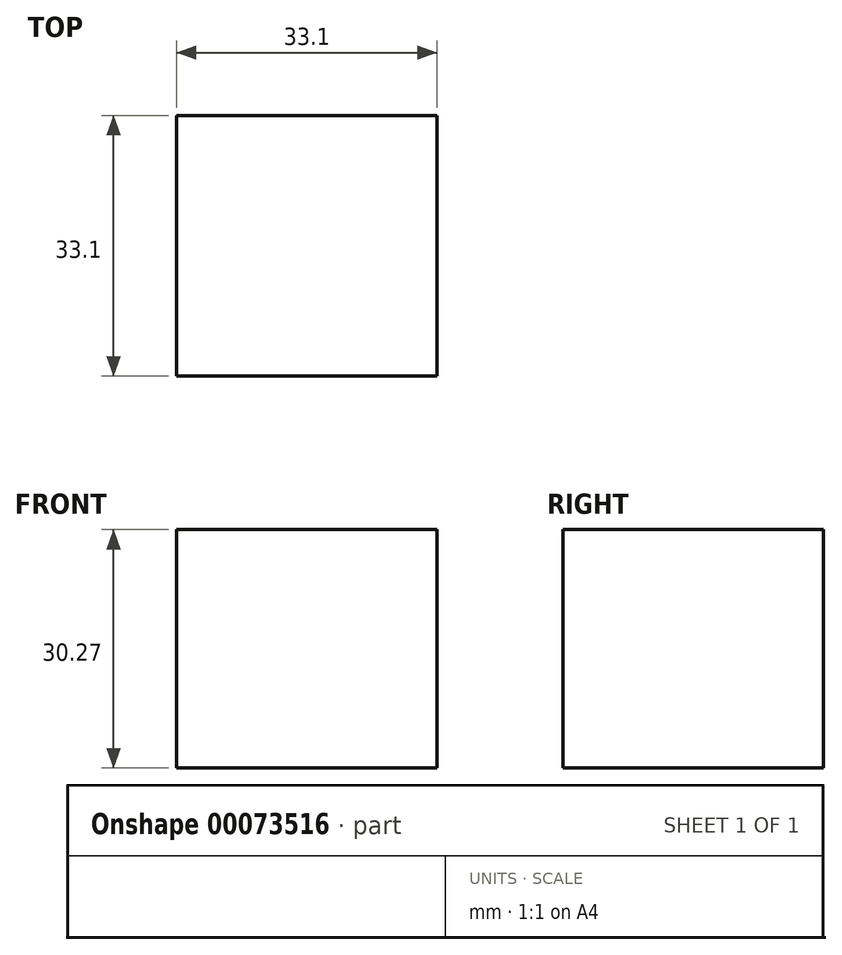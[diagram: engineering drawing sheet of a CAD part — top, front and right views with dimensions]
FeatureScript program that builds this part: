
annotation { "Feature Type Name" : "Feature", "Feature Type Description" : "" }
export const myFeature = defineFeature(function(context is Context, id is Id, definition is map)
    precondition{}
    {
        {
            var Q0;
            Q0=qCreatedBy(makeId("Top.planeOp"),FACE);
            var sketch = newSketch(context, id + "F0", { "sketchPlane" : qUnion([Q0])});
            skLineSegment(sketch, "E0.rect.bottom", {"start": v(-30.96, -10.11) * mm, "end": v(-64.06, -10.11) * mm});
            skLineSegment(sketch, "E0.rect.top", {"start": v(-30.96, 22.99) * mm, "end": v(-64.06, 22.99) * mm});
            skLineSegment(sketch, "E0.rect.left", {"start": v(-30.96, -10.11) * mm, "end": v(-30.96, 22.99) * mm});
            skLineSegment(sketch, "E0.rect.right", {"start": v(-64.06, -10.11) * mm, "end": v(-64.06, 22.99) * mm});
            skPoint(sketch, "E0.rect.middle", {"position": v(-47.5, 6.44) * mm});
            skSolve(sketch);
        }
        {
            var Q0;
            Q0=makeQuery(id+"F0.imprint","IMPRINT",FACE,{"disambiguationData":[TD([[makeQuery(id+"F0.imprint","IMPRINT",EDGE,{"derivedFrom":sQuery(id+"F0.wireOp",EDGE,"E0.rect.bottom")}),-1.0]])]});
            extrude(context, id + "F1", {"entities" : qUnion([Q0]), "depth" : 30.27 * mm});
        }
    });
